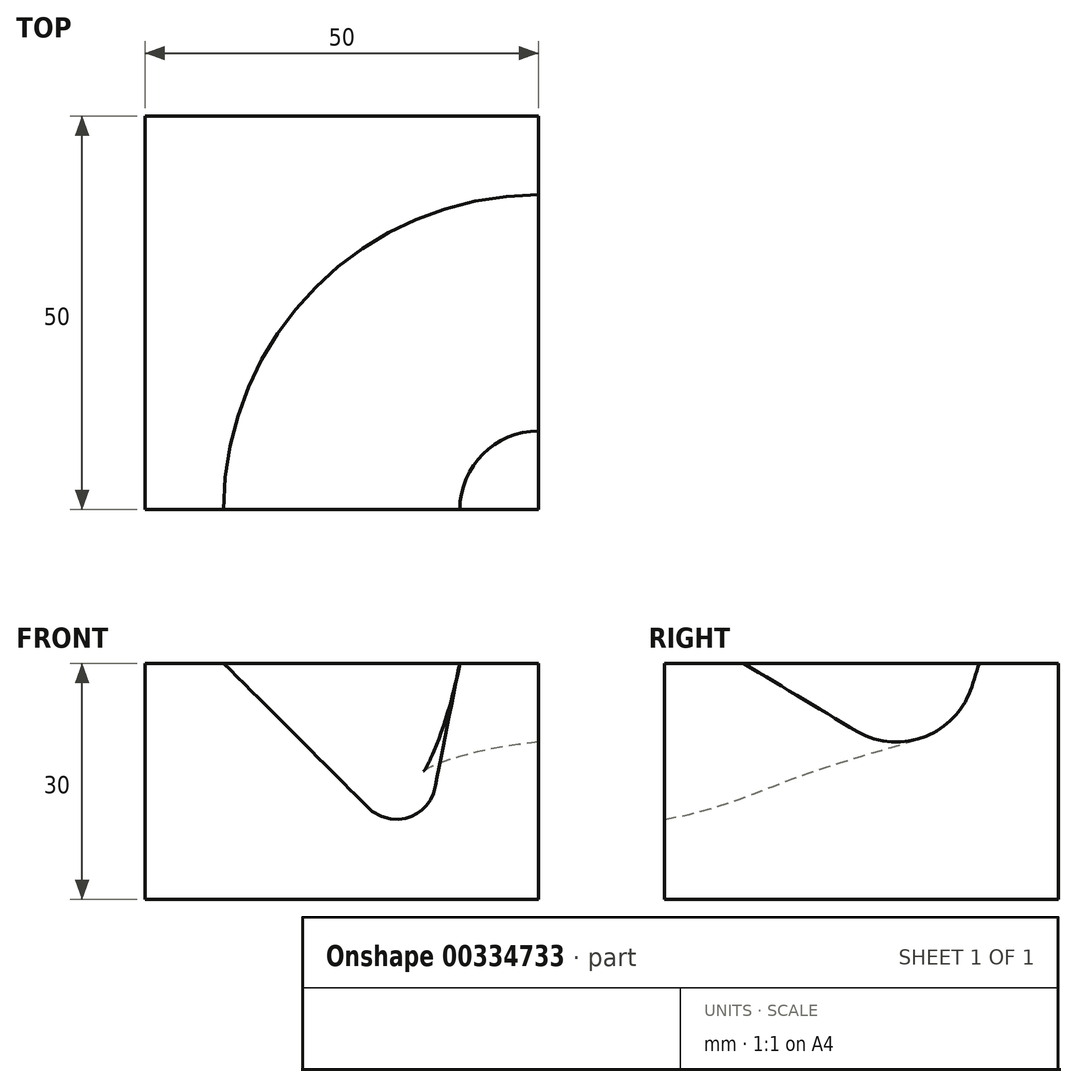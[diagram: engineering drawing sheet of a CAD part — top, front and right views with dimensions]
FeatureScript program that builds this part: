
annotation { "Feature Type Name" : "Feature", "Feature Type Description" : "" }
export const myFeature = defineFeature(function(context is Context, id is Id, definition is map)
    precondition{}
    {
        {
            var Q0;
            Q0=qCreatedBy(makeId("Top.planeOp"),FACE);
            var sketch = newSketch(context, id + "F0", { "sketchPlane" : qUnion([Q0])});
            skLineSegment(sketch, "E0.bottom", {"start": v(-26.8, 27.53) * mm, "end": v(23.2, 27.53) * mm});
            skLineSegment(sketch, "E0.top", {"start": v(-26.8, -22.47) * mm, "end": v(23.2, -22.47) * mm});
            skLineSegment(sketch, "E0.left", {"start": v(-26.8, 27.53) * mm, "end": v(-26.8, -22.47) * mm});
            skLineSegment(sketch, "E0.right", {"start": v(23.2, 27.53) * mm, "end": v(23.2, -22.47) * mm});
            skSolve(sketch);
        }
        {
            var Q0;
            Q0=makeQuery(id+"F0.imprint","IMPRINT",FACE,{"disambiguationData":[TD([[makeQuery(id+"F0.imprint","IMPRINT",EDGE,{"derivedFrom":sQuery(id+"F0.wireOp",EDGE,"E0.bottom")}),-1.0]])]});
            extrude(context, id + "F1", {"entities" : qUnion([Q0]), "depth" : 30 * mm});
        }
        {
            var Q0;
            Q0=makeQuery(id+"F1.opExtrude","SWEPT_FACE",FACE,{"disambiguationData":[OSD([sQuery(id+"F0.wireOp",EDGE,"E0.top")])]});
            var sketch = newSketch(context, id + "F2", { "sketchPlane" : qUnion([Q0])});
            skLineSegment(sketch, "E1", {"start": v(-16.8, 30) * mm, "end": v(1.6, 11.6) * mm});
            skLineSegment(sketch, "E2", {"start": v(10.03, 14.16) * mm, "end": v(13.2, 30) * mm});
            skPoint(sketch, "E3.visualSharp", {"position": v(8.2, 5) * mm});
            skArc(sketch, "E3.filletArc", {"start": v(1.6, 11.6) * mm, "mid": v(6.58, 10.36) * mm, "end": v(10.03, 14.16) * mm});
            skSolve(sketch);
        }
        {
            var Q0;
            Q0=makeQuery(id+"F1.opExtrude","SWEPT_FACE",FACE,{"disambiguationData":[OSD([sQuery(id+"F0.wireOp",EDGE,"E0.right")])]});
            var sketch = newSketch(context, id + "F3", { "sketchPlane" : qUnion([Q0])});
            skLineSegment(sketch, "E4", {"start": v(-12.47, 30) * mm, "end": v(1.85, 21.41) * mm});
            skLineSegment(sketch, "E5", {"start": v(16.48, 26.83) * mm, "end": v(17.53, 30) * mm});
            skPoint(sketch, "E6.visualSharp", {"position": v(12.53, 15) * mm});
            skArc(sketch, "E6.filletArc", {"start": v(1.85, 21.41) * mm, "mid": v(10.46, 20.6) * mm, "end": v(16.48, 26.83) * mm});
            skSolve(sketch);
        }
        {
            var Q0;
            Q0=makeQuery(id+"F1.opExtrude","CAP_FACE",FACE,{"disambiguationData":[OSD([sQuery(id+"F0.wireOp",EDGE,"E0.bottom"),sQuery(id+"F0.wireOp",EDGE,"E0.top"),sQuery(id+"F0.wireOp",EDGE,"E0.left"),sQuery(id+"F0.wireOp",EDGE,"E0.right")])],"isStart":false});
            var sketch = newSketch(context, id + "F4", { "sketchPlane" : qUnion([Q0])});
            skCircle(sketch, "E7", {"center": v(23.2, -22.47) * mm, "radius": 10 * mm});
            skCircle(sketch, "E8", {"center": v(23.2, -22.47) * mm, "radius": 40 * mm});
            skSolve(sketch);
        }
        {
            var Q1;
            {var subQ0=sQuery(id+"F2.wireOp",EDGE,"E1");Q1=makeQuery(id+"F2.imprint","IMPRINT",FACE,{"disambiguationData":[TD([[makeQuery(id+"F2.imprint","IMPRINT",EDGE,{"derivedFrom":subQ0}),1.0]])]});}
            var Q2;
            {var subQ0=sQuery(id+"F3.wireOp",EDGE,"E4");Q2=makeQuery(id+"F3.imprint","IMPRINT",FACE,{"disambiguationData":[TD([[makeQuery(id+"F3.imprint","IMPRINT",EDGE,{"derivedFrom":subQ0}),1.0]])]});}
            var Q3;
            Q3=sQuery(id+"F4.wireOp",EDGE,"E8");
            var Q4;
            Q4=sQuery(id+"F4.wireOp",EDGE,"E7");
            loft(context, id + "F5", {"operationType" : NewBodyOperationType.REMOVE, "addGuides" : true, "sheetProfilesArray" : [{ "sheetProfileEntities" : qUnion([Q1]) }, { "sheetProfileEntities" : qUnion([Q2]) }], "guidesArray" : [{ "guideEntities" : qUnion([Q3]), "guideDerivativeType" : LoftGuideDerivativeType.DEFAULT, "guideDerivativeMagnitude" : 1 }, { "guideEntities" : qUnion([Q4]), "guideDerivativeType" : LoftGuideDerivativeType.DEFAULT, "guideDerivativeMagnitude" : 1 }]});
        }
    });
